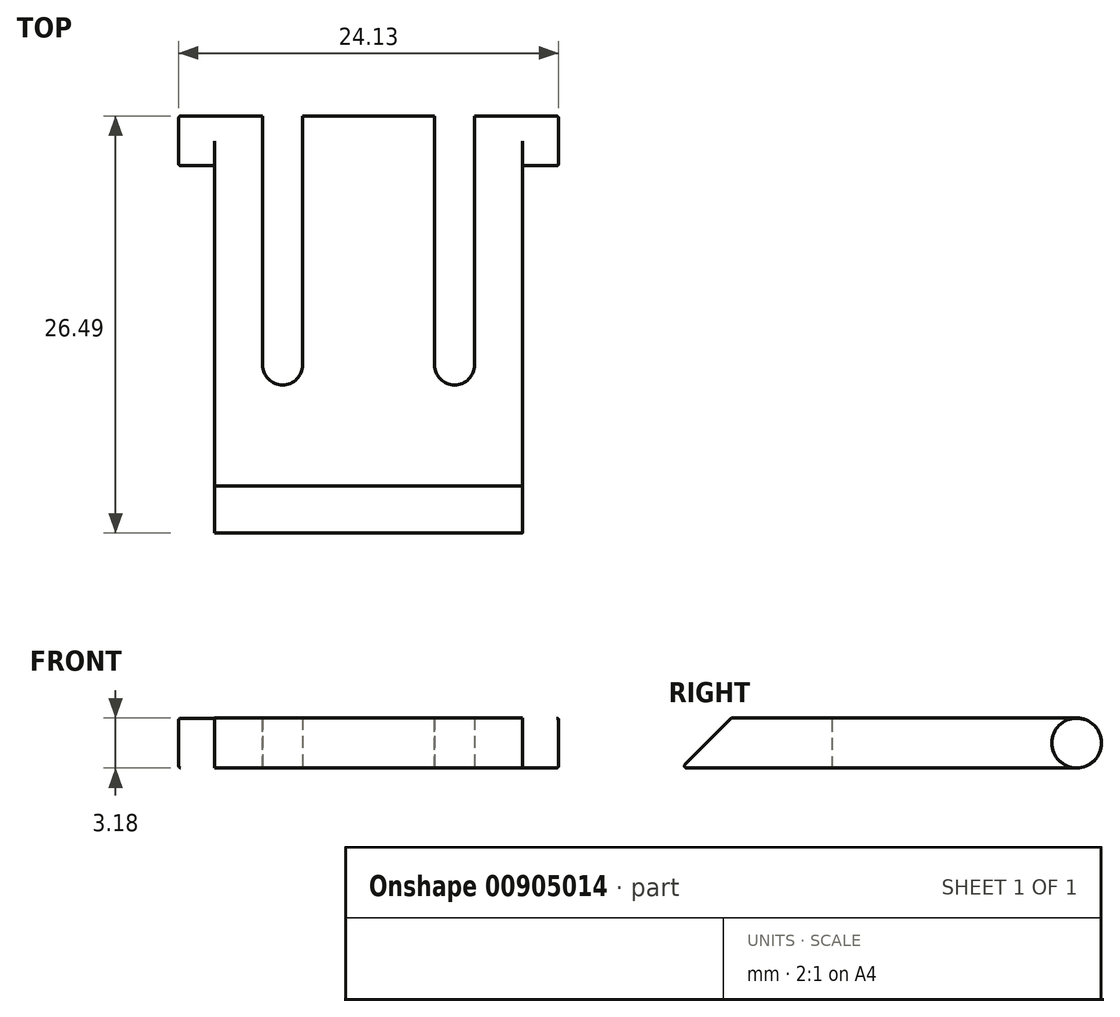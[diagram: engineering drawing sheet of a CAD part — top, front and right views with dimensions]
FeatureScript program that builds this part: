
annotation { "Feature Type Name" : "Feature", "Feature Type Description" : "" }
export const myFeature = defineFeature(function(context is Context, id is Id, definition is map)
    precondition{}
    {
        {
            var Q0;
            Q0=qCreatedBy(makeId("Top.planeOp"),FACE);
            var sketch = newSketch(context, id + "F0", { "sketchPlane" : qUnion([Q0])});
            skLineSegment(sketch, "E0", {"start": v(0, 0) * mm, "end": v(3.05, 0) * mm});
            skLineSegment(sketch, "E1", {"start": v(3.05, 0) * mm, "end": v(3.05, -17.09) * mm});
            skLineSegment(sketch, "E2", {"start": v(3.05, -17.09) * mm, "end": v(5.59, -17.09) * mm});
            skLineSegment(sketch, "E3", {"start": v(5.59, -17.09) * mm, "end": v(5.59, 0) * mm});
            skLineSegment(sketch, "E4", {"start": v(5.59, 0) * mm, "end": v(13.97, 0) * mm});
            skLineSegment(sketch, "E5", {"start": v(13.97, 0) * mm, "end": v(13.97, -17.09) * mm});
            skLineSegment(sketch, "E6", {"start": v(13.97, -17.09) * mm, "end": v(16.5, -17.09) * mm});
            skLineSegment(sketch, "E7", {"start": v(16.5, -17.09) * mm, "end": v(16.5, 0) * mm});
            skLineSegment(sketch, "E8", {"start": v(16.5, 0) * mm, "end": v(19.56, 0) * mm});
            skLineSegment(sketch, "E9", {"start": v(19.56, 0) * mm, "end": v(19.56, -26.67) * mm});
            skLineSegment(sketch, "E10", {"start": v(19.56, -26.67) * mm, "end": v(0, -26.67) * mm});
            skLineSegment(sketch, "E11", {"start": v(0, -26.67) * mm, "end": v(0, 0) * mm});
            skSolve(sketch);
        }
        {
            var Q0;
            Q0=makeQuery(id+"F0.imprint","IMPRINT",FACE,{"disambiguationData":[TD([[makeQuery(id+"F0.imprint","IMPRINT",EDGE,{"derivedFrom":sQuery(id+"F0.wireOp",EDGE,"E0")}),-1.0]])]});
            extrude(context, id + "F1", {"entities" : qUnion([Q0]), "depth" : 3.17 * mm, "offsetDistance" : 25.4 * mm});
        }
        {
            var Q0;
            Q0=makeQuery(id+"F1.opExtrude","CAP_EDGE",EDGE,{"disambiguationData":[OSD([sQuery(id+"F0.wireOp",EDGE,"E10")])],"isStart":false});
            chamfer(context, id + "F2", {"entities" : qUnion([Q0]), "width" : 3.17 * mm, "tangentPropagation" : true});
        }
        {
            var Q0;
            Q0=makeQuery(id+"F1.opExtrude","CAP_EDGE",EDGE,{"disambiguationData":[OSD([sQuery(id+"F0.wireOp",EDGE,"E8")])],"isStart":false});
            var Q1;
            Q1=makeQuery(id+"F1.opExtrude","CAP_EDGE",EDGE,{"disambiguationData":[OSD([sQuery(id+"F0.wireOp",EDGE,"E4")])],"isStart":false});
            var Q2;
            Q2=makeQuery(id+"F1.opExtrude","CAP_EDGE",EDGE,{"disambiguationData":[OSD([sQuery(id+"F0.wireOp",EDGE,"E8")])],"isStart":true});
            var Q3;
            Q3=makeQuery(id+"F1.opExtrude","CAP_EDGE",EDGE,{"disambiguationData":[OSD([sQuery(id+"F0.wireOp",EDGE,"E4")])],"isStart":true});
            var Q4;
            Q4=makeQuery(id+"F1.opExtrude","CAP_EDGE",EDGE,{"disambiguationData":[OSD([sQuery(id+"F0.wireOp",EDGE,"E0")])],"isStart":true});
            var Q5;
            Q5=makeQuery(id+"F1.opExtrude","CAP_EDGE",EDGE,{"disambiguationData":[OSD([sQuery(id+"F0.wireOp",EDGE,"E0")])],"isStart":false});
            fillet(context, id + "F3", {"entities" : qUnion([Q0, Q1, Q2, Q3, Q4, Q5]), "radius" : 1.59 * mm, "tangentPropagation" : true, "allowEdgeOverflow" : false});
        }
        {
            var Q0;
            Q0=makeQuery(id+"F1.opExtrude","SWEPT_FACE",FACE,{"disambiguationData":[OSD([sQuery(id+"F0.wireOp",EDGE,"E9")])]});
            var sketch = newSketch(context, id + "F4", { "sketchPlane" : qUnion([Q0])});
            skCircle(sketch, "E12", {"center": v(-1.59, 1.59) * mm, "radius": 1.58 * mm});
            skSolve(sketch);
        }
        {
            var Q0;
            Q0=makeQuery(id+"F4.imprint","IMPRINT",FACE,{"disambiguationData":[TD([[makeQuery(id+"F4.imprint","IMPRINT",EDGE,{"derivedFrom":sQuery(id+"F4.wireOp",EDGE,"E12")}),1.0]])]});
            extrude(context, id + "F5", {"entities" : qUnion([Q0]), "operationType" : NewBodyOperationType.ADD, "depth" : 2.3 * mm, "offsetDistance" : 25.4 * mm});
        }
        {
            var Q0;
            Q0=makeQuery(id+"F1.opExtrude","SWEPT_FACE",FACE,{"disambiguationData":[OSD([sQuery(id+"F0.wireOp",EDGE,"E11")])]});
            var sketch = newSketch(context, id + "F6", { "sketchPlane" : qUnion([Q0])});
            skCircle(sketch, "E13", {"center": v(1.59, 1.59) * mm, "radius": 1.58 * mm});
            skSolve(sketch);
        }
        {
            var Q0;
            Q0=makeQuery(id+"F6.imprint","IMPRINT",FACE,{"disambiguationData":[TD([[makeQuery(id+"F6.imprint","IMPRINT",EDGE,{"derivedFrom":sQuery(id+"F6.wireOp",EDGE,"E13")}),1.0]])]});
            extrude(context, id + "F7", {"entities" : qUnion([Q0]), "operationType" : NewBodyOperationType.ADD, "depth" : 2.3 * mm, "offsetDistance" : 25.4 * mm});
        }
        {
            var Q0;
            Q0=makeQuery(id+"F1.opExtrude","SWEPT_EDGE",EDGE,{"disambiguationData":[OSD([sQuery(id+"F0.wireOp",EDGE,"E5"),sQuery(id+"F0.wireOp",EDGE,"E6")])]});
            var Q1;
            Q1=makeQuery(id+"F1.opExtrude","SWEPT_EDGE",EDGE,{"disambiguationData":[OSD([sQuery(id+"F0.wireOp",EDGE,"E1"),sQuery(id+"F0.wireOp",EDGE,"E2")])]});
            var Q2;
            Q2=makeQuery(id+"F1.opExtrude","SWEPT_EDGE",EDGE,{"disambiguationData":[OSD([sQuery(id+"F0.wireOp",EDGE,"E2"),sQuery(id+"F0.wireOp",EDGE,"E3")])]});
            var Q3;
            Q3=makeQuery(id+"F1.opExtrude","SWEPT_EDGE",EDGE,{"disambiguationData":[OSD([sQuery(id+"F0.wireOp",EDGE,"E6"),sQuery(id+"F0.wireOp",EDGE,"E7")])]});
            fillet(context, id + "F8", {"entities" : qUnion([Q0, Q1, Q2, Q3]), "radius" : 1.27 * mm, "tangentPropagation" : true, "allowEdgeOverflow" : false});
        }
        {
            var Q0;
            {var subQ0=sQuery(id+"F0.wireOp",EDGE,"E10");Q0=makeQuery(id+"F2.opChamfer","BLEND_EDGE",EDGE,{"blendedFrom":[makeQuery(id+"F1.opExtrude","CAP_EDGE",EDGE,{"disambiguationData":[OSD([subQ0])],"isStart":false}),makeQuery(id+"F1.opExtrude","CAP_FACE",FACE,{"disambiguationData":[OSD([sQuery(id+"F0.wireOp",EDGE,"E0"),sQuery(id+"F0.wireOp",EDGE,"E1"),sQuery(id+"F0.wireOp",EDGE,"E2"),sQuery(id+"F0.wireOp",EDGE,"E3"),sQuery(id+"F0.wireOp",EDGE,"E4"),sQuery(id+"F0.wireOp",EDGE,"E5"),sQuery(id+"F0.wireOp",EDGE,"E6"),sQuery(id+"F0.wireOp",EDGE,"E7"),sQuery(id+"F0.wireOp",EDGE,"E8"),sQuery(id+"F0.wireOp",EDGE,"E9"),subQ0,sQuery(id+"F0.wireOp",EDGE,"E11")])],"isStart":true})],"blendedInto":[makeQuery(id+"F1.opExtrude","CAP_FACE",FACE,{"disambiguationData":[OSD([sQuery(id+"F0.wireOp",EDGE,"E0"),sQuery(id+"F0.wireOp",EDGE,"E1"),sQuery(id+"F0.wireOp",EDGE,"E2"),sQuery(id+"F0.wireOp",EDGE,"E3"),sQuery(id+"F0.wireOp",EDGE,"E4"),sQuery(id+"F0.wireOp",EDGE,"E5"),sQuery(id+"F0.wireOp",EDGE,"E6"),sQuery(id+"F0.wireOp",EDGE,"E7"),sQuery(id+"F0.wireOp",EDGE,"E8"),sQuery(id+"F0.wireOp",EDGE,"E9"),subQ0,sQuery(id+"F0.wireOp",EDGE,"E11")])],"isStart":true})]});}
            fillet(context, id + "F9", {"entities" : qUnion([Q0]), "radius" : 0.13 * mm, "tangentPropagation" : true, "allowEdgeOverflow" : false});
        }
        {
            var Q0;
            Q0=makeQuery(id+"F5.opExtrude","CAP_EDGE",EDGE,{"disambiguationData":[OSD([sQuery(id+"F4.wireOp",EDGE,"E12")])],"isStart":false});
            var Q1;
            Q1=makeQuery(id+"F7.opExtrude","CAP_EDGE",EDGE,{"disambiguationData":[OSD([sQuery(id+"F6.wireOp",EDGE,"E13")])],"isStart":false});
            fillet(context, id + "F10", {"entities" : qUnion([Q0, Q1]), "radius" : 0.13 * mm, "tangentPropagation" : true, "allowEdgeOverflow" : false});
        }
    });
